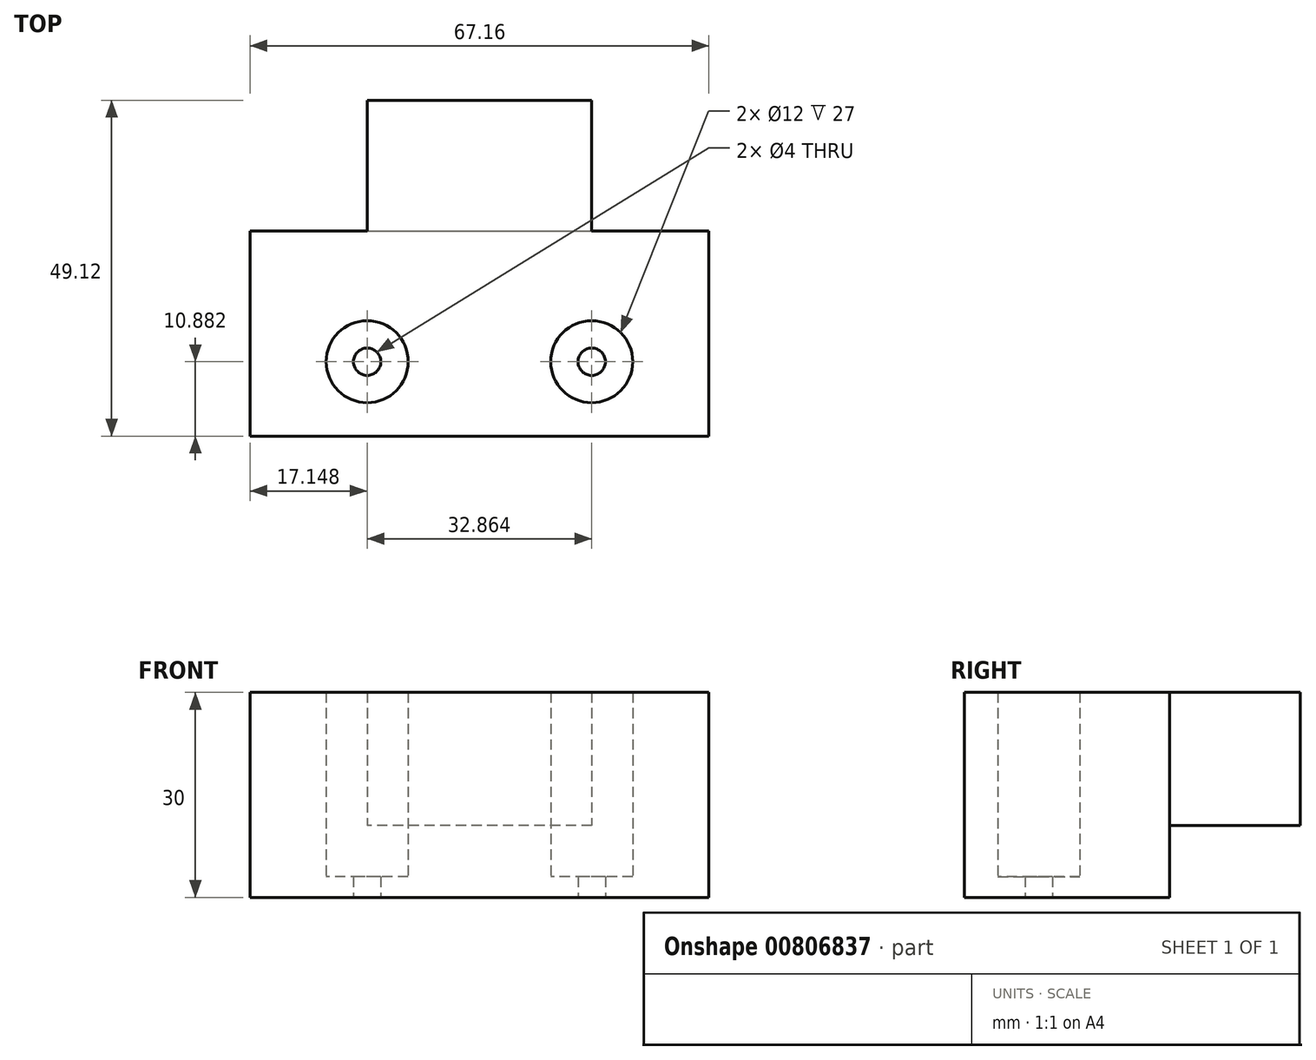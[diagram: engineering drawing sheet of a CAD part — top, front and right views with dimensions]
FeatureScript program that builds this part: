
annotation { "Feature Type Name" : "Feature", "Feature Type Description" : "" }
export const myFeature = defineFeature(function(context is Context, id is Id, definition is map)
    precondition{}
    {
        {
            var Q0;
            Q0=qCreatedBy(makeId("Top.planeOp"),FACE);
            var sketch = newSketch(context, id + "F0", { "sketchPlane" : qUnion([Q0])});
            skLineSegment(sketch, "E0.bottom", {"start": v(33.58, 30) * mm, "end": v(-33.58, 30) * mm});
            skLineSegment(sketch, "E0.top", {"start": v(33.58, -30) * mm, "end": v(-33.58, -30) * mm});
            skLineSegment(sketch, "E0.left", {"start": v(33.58, 30) * mm, "end": v(33.58, -30) * mm});
            skLineSegment(sketch, "E0.right", {"start": v(-33.58, 30) * mm, "end": v(-33.58, -30) * mm});
            skPoint(sketch, "E0.middle", {"position": v(0, 0) * mm});
            skLineSegment(sketch, "E1.bottom", {"start": v(-33.58, 30) * mm, "end": v(33.58, 30) * mm});
            skLineSegment(sketch, "E1.top", {"start": v(-33.58, 0) * mm, "end": v(33.58, 0) * mm});
            skLineSegment(sketch, "E1.left", {"start": v(-33.58, 30) * mm, "end": v(-33.58, 0) * mm});
            skLineSegment(sketch, "E1.right", {"start": v(33.58, 30) * mm, "end": v(33.58, 0) * mm});
            skLineSegment(sketch, "E2.bottom", {"start": v(16.43, -19.12) * mm, "end": v(-16.43, -19.12) * mm});
            skLineSegment(sketch, "E2.top", {"start": v(16.43, 19.12) * mm, "end": v(-16.43, 19.12) * mm});
            skLineSegment(sketch, "E2.left", {"start": v(16.43, -19.12) * mm, "end": v(16.43, 19.12) * mm});
            skLineSegment(sketch, "E2.right", {"start": v(-16.43, -19.12) * mm, "end": v(-16.43, 19.12) * mm});
            skCircle(sketch, "E3", {"center": v(16.43, -19.12) * mm, "radius": 6 * mm});
            skCircle(sketch, "E4", {"center": v(-16.43, -19.12) * mm, "radius": 6 * mm});
            skCircle(sketch, "E5", {"center": v(-16.43, -19.12) * mm, "radius": 2 * mm});
            skCircle(sketch, "E6", {"center": v(16.43, -19.12) * mm, "radius": 2 * mm});
            skSolve(sketch);
        }
        {
            var Q0;
            Q0=makeQuery(id+"F0.imprint","IMPRINT",FACE,{"disambiguationData":[TD([[makeQuery(id+"F0.imprint","IMPRINT",EDGE,{"derivedFrom":sQuery(id+"F0.wireOp",EDGE,"E1.bottom")}),-1.0]])]});
            var Q1;
            {var subQ5=sQuery(id+"F0.wireOp",EDGE,"E2.top");Q1=makeQuery(id+"F0.imprint","IMPRINT",FACE,{"disambiguationData":[TD([[makeQuery(id+"F0.imprint","IMPRINT",EDGE,{"derivedFrom":subQ5}),1.0]])]});}
            extrude(context, id + "F1", {"entities" : qUnion([Q0, Q1]), "depth" : 30 * mm, "offsetDistance" : 25 * mm});
        }
        {
            var Q0;
            {var subQ1=sQuery(id+"F0.wireOp",EDGE,"E1.top");var subQ5=sQuery(id+"F0.wireOp",EDGE,"E2.right");var subQ6=makeQuery(id+"F0.imprint","INTERSECT",VERTEX,{"derivedFrom":[subQ1,subQ5]});Q0=makeQuery(id+"F0.imprint","IMPRINT",FACE,{"disambiguationData":[TD([[makeQuery(id+"F0.imprint","IMPRINT",EDGE,{"disambiguationData":[TD([[subQ6,-1.0]])],"derivedFrom":subQ1}),-1.0]])]});}
            var Q1;
            Q1=makeQuery(id+"F0.imprint","IMPRINT",FACE,{"disambiguationData":[TD([[makeQuery(id+"F0.imprint","IMPRINT",EDGE,{"derivedFrom":sQuery(id+"F0.wireOp",EDGE,"E0.top")}),-1.0]])]});
            extrude(context, id + "F2", {"entities" : qUnion([Q0, Q1]), "operationType" : NewBodyOperationType.ADD, "depth" : 30 * mm, "offsetDistance" : 25 * mm});
        }
        {
            var Q0;
            {var subQ0=sQuery(id+"F0.wireOp",EDGE,"E4");var subQ1=sQuery(id+"F0.wireOp",EDGE,"E2.bottom");var subQ2=makeQuery(id+"F0.imprint","INTERSECT",VERTEX,{"derivedFrom":[subQ1,subQ0]});Q0=makeQuery(id+"F0.imprint","IMPRINT",FACE,{"disambiguationData":[TD([[makeQuery(id+"F0.imprint","IMPRINT",EDGE,{"disambiguationData":[TD([[subQ2,-1.0]])],"derivedFrom":subQ1}),1.0]])]});}
            var Q1;
            {var subQ0=sQuery(id+"F0.wireOp",EDGE,"E4");var subQ1=sQuery(id+"F0.wireOp",EDGE,"E2.bottom");var subQ2=makeQuery(id+"F0.imprint","INTERSECT",VERTEX,{"derivedFrom":[subQ1,subQ0]});Q1=makeQuery(id+"F0.imprint","IMPRINT",FACE,{"disambiguationData":[TD([[makeQuery(id+"F0.imprint","IMPRINT",EDGE,{"disambiguationData":[TD([[subQ2,-1.0]])],"derivedFrom":subQ1}),-1.0]])]});}
            var Q2;
            {var subQ0=sQuery(id+"F0.wireOp",EDGE,"E6");var subQ1=sQuery(id+"F0.wireOp",EDGE,"E2.bottom");var subQ2=makeQuery(id+"F0.imprint","INTERSECT",VERTEX,{"derivedFrom":[subQ1,subQ0]});Q2=makeQuery(id+"F0.imprint","IMPRINT",FACE,{"disambiguationData":[TD([[makeQuery(id+"F0.imprint","IMPRINT",EDGE,{"disambiguationData":[TD([[subQ2,-1.0]])],"derivedFrom":subQ1}),-1.0]])]});}
            var Q3;
            {var subQ0=sQuery(id+"F0.wireOp",EDGE,"E6");var subQ1=sQuery(id+"F0.wireOp",EDGE,"E2.bottom");var subQ2=makeQuery(id+"F0.imprint","INTERSECT",VERTEX,{"derivedFrom":[subQ1,subQ0]});Q3=makeQuery(id+"F0.imprint","IMPRINT",FACE,{"disambiguationData":[TD([[makeQuery(id+"F0.imprint","IMPRINT",EDGE,{"disambiguationData":[TD([[subQ2,-1.0]])],"derivedFrom":subQ1}),1.0]])]});}
            extrude(context, id + "F3", {"entities" : qUnion([Q0, Q1, Q2, Q3]), "operationType" : NewBodyOperationType.ADD, "depth" : 3 * mm, "offsetDistance" : 25 * mm});
        }
        {
            var Q0;
            Q0=makeQuery(id+"F0.imprint","IMPRINT",FACE,{"disambiguationData":[TD([[makeQuery(id+"F0.imprint","IMPRINT",EDGE,{"derivedFrom":sQuery(id+"F0.wireOp",EDGE,"E1.bottom")}),-1.0]])]});
            var Q1;
            {var subQ5=sQuery(id+"F0.wireOp",EDGE,"E2.top");Q1=makeQuery(id+"F0.imprint","IMPRINT",FACE,{"disambiguationData":[TD([[makeQuery(id+"F0.imprint","IMPRINT",EDGE,{"derivedFrom":subQ5}),1.0]])]});}
            extrude(context, id + "F4", {"entities" : qUnion([Q0, Q1]), "operationType" : NewBodyOperationType.REMOVE, "oppositeDirection" : true, "depth" : -10.5 * mm, "offsetDistance" : 25 * mm});
        }
    });
